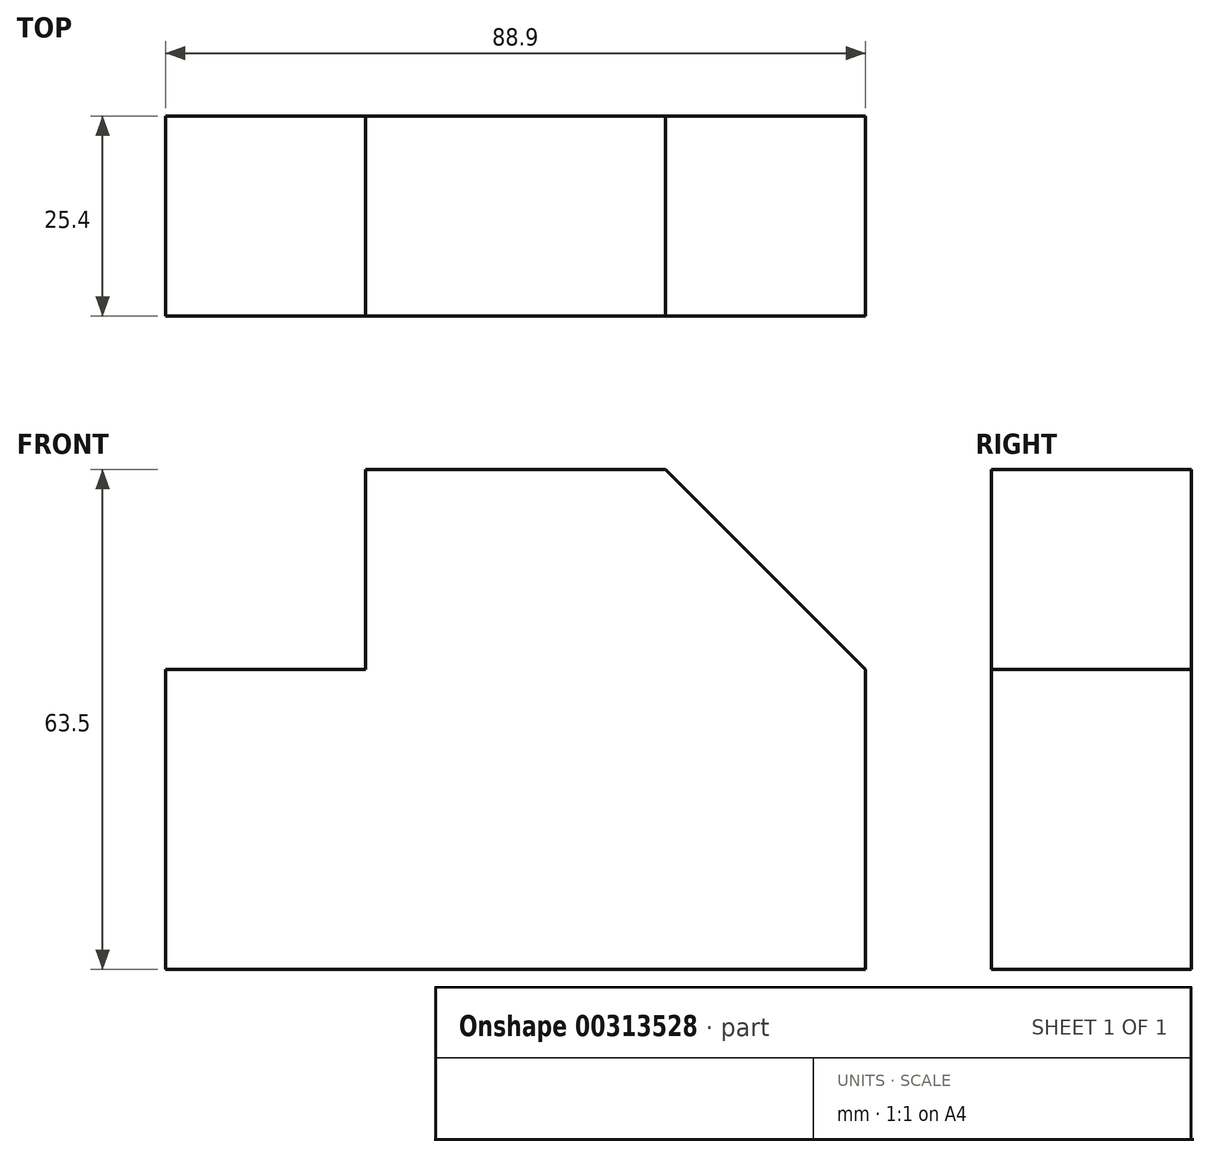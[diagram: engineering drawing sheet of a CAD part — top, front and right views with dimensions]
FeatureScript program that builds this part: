
annotation { "Feature Type Name" : "Feature", "Feature Type Description" : "" }
export const myFeature = defineFeature(function(context is Context, id is Id, definition is map)
    precondition{}
    {
        {
            var Q0;
            Q0=qCreatedBy(makeId("Front.planeOp"),FACE);
            var sketch = newSketch(context, id + "F0", { "sketchPlane" : qUnion([Q0])});
            skLineSegment(sketch, "E0", {"start": v(-46.6, -39.45) * mm, "end": v(42.3, -39.45) * mm});
            skLineSegment(sketch, "E1", {"start": v(42.3, -39.45) * mm, "end": v(42.3, -1.35) * mm});
            skLineSegment(sketch, "E2", {"start": v(42.3, -1.35) * mm, "end": v(16.9, 24.05) * mm});
            skLineSegment(sketch, "E3", {"start": v(16.9, 24.05) * mm, "end": v(-21.2, 24.05) * mm});
            skLineSegment(sketch, "E4", {"start": v(-21.2, 24.05) * mm, "end": v(-21.2, -1.35) * mm});
            skLineSegment(sketch, "E5", {"start": v(-21.2, -1.35) * mm, "end": v(-46.6, -1.35) * mm});
            skLineSegment(sketch, "E6", {"start": v(-46.6, -1.35) * mm, "end": v(-46.6, -39.45) * mm});
            skSolve(sketch);
        }
        {
            var Q0;
            Q0=makeQuery(id+"F0.imprint","IMPRINT",FACE,{"disambiguationData":[TD([[makeQuery(id+"F0.imprint","IMPRINT",EDGE,{"derivedFrom":sQuery(id+"F0.wireOp",EDGE,"E0")}),1.0]])]});
            extrude(context, id + "F1", {"entities" : qUnion([Q0]), "depth" : 25.4 * mm});
        }
    });
